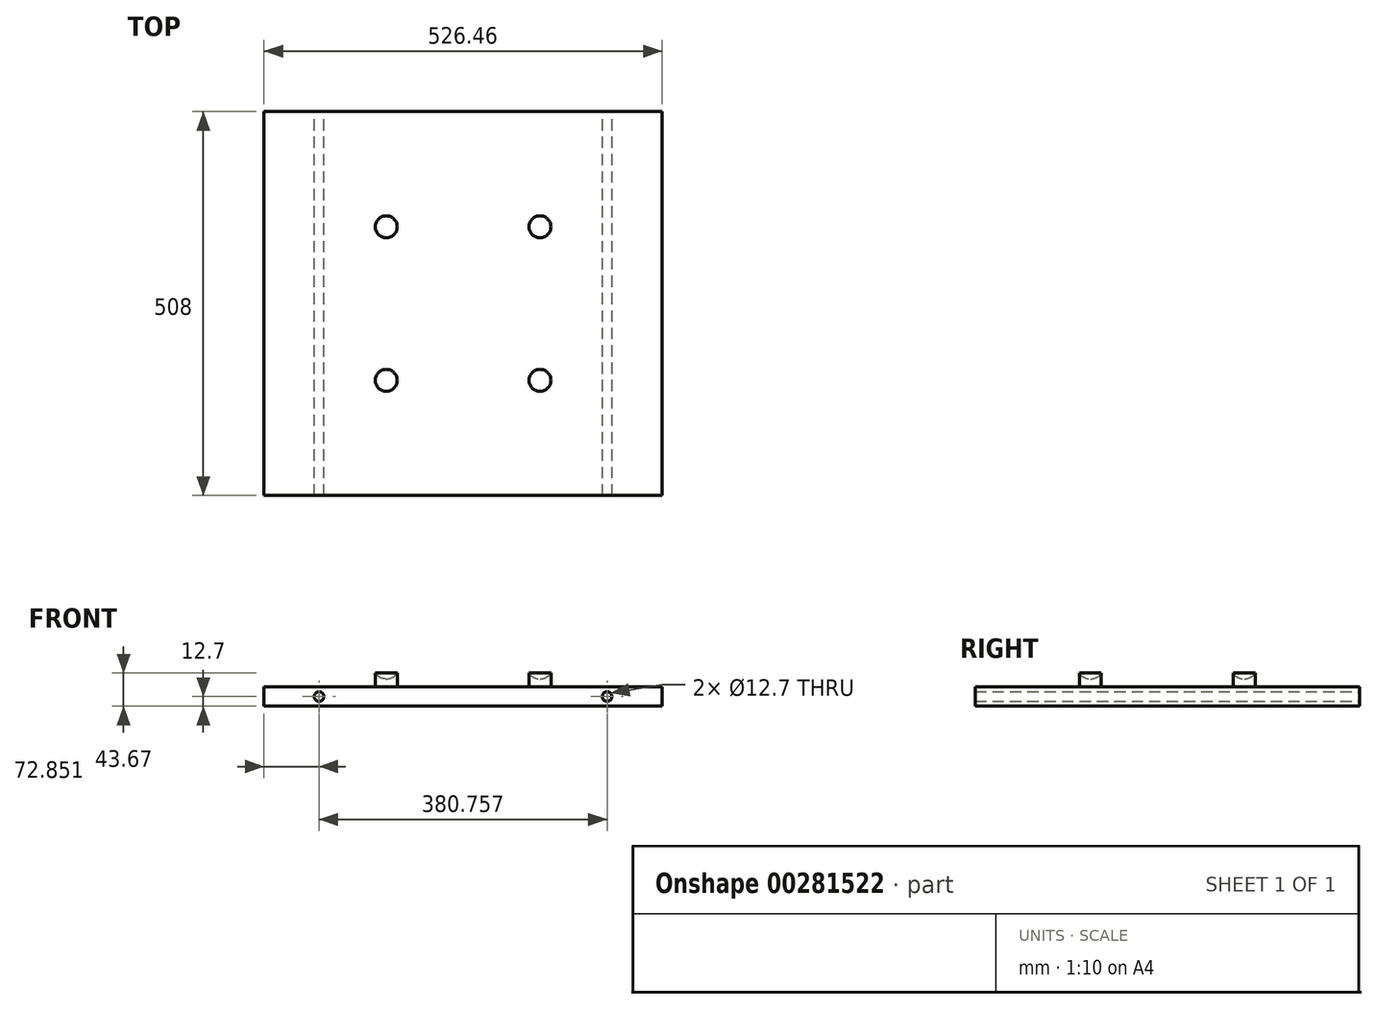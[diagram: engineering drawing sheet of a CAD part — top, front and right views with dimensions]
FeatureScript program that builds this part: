
annotation { "Feature Type Name" : "Feature", "Feature Type Description" : "" }
export const myFeature = defineFeature(function(context is Context, id is Id, definition is map)
    precondition{}
    {
        {
            var Q0;
            Q0=qCreatedBy(makeId("Front.planeOp"),FACE);
            var sketch = newSketch(context, id + "F0", { "sketchPlane" : qUnion([Q0])});
            skLineSegment(sketch, "E0.bottom", {"start": v(-244.77, 12.7) * mm, "end": v(263.23, 12.7) * mm});
            skLineSegment(sketch, "E0.top", {"start": v(-244.77, -12.7) * mm, "end": v(263.23, -12.7) * mm});
            skLineSegment(sketch, "E0.left", {"start": v(-244.77, 12.7) * mm, "end": v(-244.77, -12.7) * mm});
            skLineSegment(sketch, "E0.right", {"start": v(263.23, 12.7) * mm, "end": v(263.23, -12.7) * mm});
            skCircle(sketch, "E1", {"center": v(-190.38, 0) * mm, "radius": 6.35 * mm});
            skCircle(sketch, "E2.MirrorC", {"center": v(190.38, 0) * mm, "radius": 6.35 * mm});
            skSolve(sketch);
        }
        {
            var Q0;
            Q0 = qSketchRegion(id + "F0", true);
            extrude(context, id + "F1", {"entities" : qUnion([Q0]), "endBound" : BoundingType.SYMMETRIC, "depth" : 508 * mm});
        }
        {
            var Q0;
            Q0=qCreatedBy(makeId("Front.planeOp"),FACE);
            cPlane(context, id + "F2", {"entities" : qUnion([Q0]), "cplaneType" : CPlaneType.OFFSET, "offset" : 101.6 * mm, "width" : 152.4 * mm, "height" : 152.4 * mm});
        }
        {
            var Q0;
            Q0=qCreatedBy(id+"F2.planeOp",FACE);
            var sketch = newSketch(context, id + "F3", { "sketchPlane" : qUnion([Q0])});
            skLineSegment(sketch, "E3", {"start": v(-116.15, 30.97) * mm, "end": v(-116.15, 10.77) * mm});
            skLineSegment(sketch, "E4", {"start": v(-116.15, 10.77) * mm, "end": v(-101.6, 10.77) * mm});
            skArc(sketch, "E5", {"start": v(-116.15, 30.97) * mm, "mid": v(-109.83, 25.33) * mm, "end": v(-101.6, 23.29) * mm});
            skLineSegment(sketch, "E6", {"start": v(-101.6, 23.29) * mm, "end": v(-101.6, 10.77) * mm});
            skLineSegment(sketch, "E7", {"start": v(-74.86, 23.29) * mm, "end": v(0, 23.29) * mm});
            skSolve(sketch);
        }
        {
            var Q0;
            Q0 = qSketchRegion(id + "F3", true);
            var Q1;
            Q1=sQuery(id+"F3.wireOp",EDGE,"E6");
            revolve(context, id + "F4", {"operationType" : NewBodyOperationType.ADD, "entities" : qUnion([Q0]), "axis" : qUnion([Q1]), "revolveType" : RevolveType.FULL});
        }
        {
            var Q0;
            Q0=makeQuery(id+"F1.opExtrude","SWEPT_BODY",BODY,{"disambiguationData":[OSD([sQuery(id+"F0.wireOp",EDGE,"E0.bottom"),sQuery(id+"F0.wireOp",EDGE,"E0.top"),sQuery(id+"F0.wireOp",EDGE,"E0.left"),sQuery(id+"F0.wireOp",EDGE,"E0.right"),sQuery(id+"F0.wireOp",EDGE,"E1"),sQuery(id+"F0.wireOp",EDGE,"E2.MirrorC")])]});
            var Q1;
            Q1=qCreatedBy(makeId("Right.planeOp"),FACE);
            mirror(context, id + "F5", {"operationType" : NewBodyOperationType.ADD, "entities" : qUnion([Q0]), "mirrorPlane" : qUnion([Q1])});
        }
        {
            var Q0;
            Q0=makeQuery(id+"F1.opExtrude","SWEPT_BODY",BODY,{"disambiguationData":[OSD([sQuery(id+"F0.wireOp",EDGE,"E0.bottom"),sQuery(id+"F0.wireOp",EDGE,"E0.top"),sQuery(id+"F0.wireOp",EDGE,"E0.left"),sQuery(id+"F0.wireOp",EDGE,"E0.right"),sQuery(id+"F0.wireOp",EDGE,"E1"),sQuery(id+"F0.wireOp",EDGE,"E2.MirrorC")])]});
            var Q1;
            Q1=qCreatedBy(makeId("Front.planeOp"),FACE);
            mirror(context, id + "F6", {"operationType" : NewBodyOperationType.ADD, "entities" : qUnion([Q0]), "mirrorPlane" : qUnion([Q1])});
        }
    });
